# Revit family: Sanitary_Taps-Mixers_hansgrohe_72518AUS-Rebris-S-Single-lever-basin-mix_new
name_source: partatom
category: Plumbing Fixtures
revit_build: Autodesk Revit 2018 (Build: 20170223_1515(x64)
units: mm (PartAtom-declared; Revit-internal decimal feet)

## family parameters
Always vertical = No
Cut with Voids When Loaded = No
OmniClass Number = 23.45.55.17
OmniClass Title = Mixing Faucets
Part Type = Normal
Room Calculation Point = No
Round Connector Dimension = Use Diameter
Shared = No
Work Plane-Based = Yes

## types (2) — shared parameters
Always visible = Yes
BIMobject category = Taps & Mixers
Cold Water Inlet = 10 mm
Cold Water Inlet Description = Cold Water Inlet 9.5mm
Default Elevation = 1219.2 mm  [stored 4 ft]
Description = Rebris S Single lever basin mixer 110 without waste set
Design country = Germany
EAN code = 4059625420461
Edition number = 1
GTIN code = https://4059625420461
Hot Water Inlet = 10 mm
Hot Water Inlet Description = Hot Water Inlet 9.5mm
IFC Classification = Valve
Manufacturer = Hansgrohe
Manufacturer country = Germany
Manufacturer name = hansgrohe
Model = 72518AUS
OmniClass Code = 23-31 11 00
OmniClass Description = Faucets
Product Guid = f9417914-4a97-4107-8df5-84897a8cbe42
Product SKU = 72518AUS
Product data url = https://bimobject.com
Product family = Rebris S
Product group = Basin mixers
Product name = 72518AUS Rebris S Single lever basin mixer 110 without waste set
QR code = https://bimobject.com
UNSPSC Code = 301815
URL = https://www.hansgrohe.com
Weight Net (Kg) = 1.5

## per-type parameters (varying)
| type | Material 1 |
| 673 Matte Black | Hansgrohe - Metal - 673 Matte Black |
| 003 Chrome | Hansgrohe - Metal - 003 Chrome |

note: [stored X ft] marks values corroborated as IEEE doubles in the binary element streams (Revit-internal decimal feet)

## geometry (parser evidence)
native form markers: Sweep x2
no freeform markers — native parametric forms only
